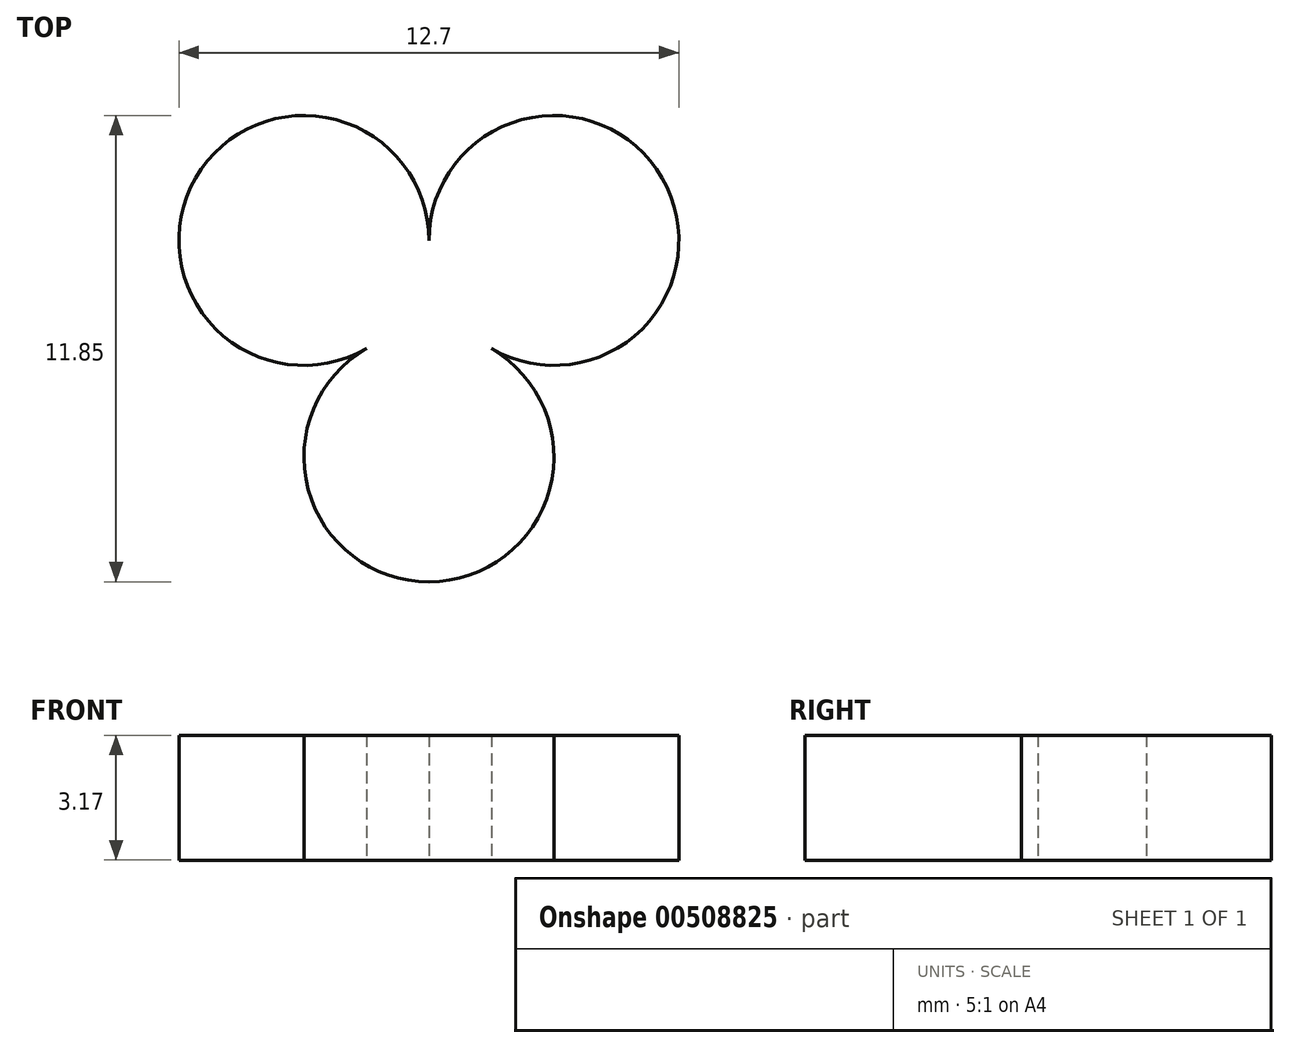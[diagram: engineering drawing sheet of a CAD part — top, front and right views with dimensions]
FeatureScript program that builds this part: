
annotation { "Feature Type Name" : "Feature", "Feature Type Description" : "" }
export const myFeature = defineFeature(function(context is Context, id is Id, definition is map)
    precondition{}
    {
        {
            var Q0;
            Q0=qCreatedBy(makeId("Right.planeOp"),FACE);
            var sketch = newSketch(context, id + "F0", { "sketchPlane" : qUnion([Q0])});
            skLineSegment(sketch, "E0", {"start": v(0, 0) * mm, "end": v(0, 179.6) * mm});
            skLineSegment(sketch, "E1", {"start": v(0, 179.6) * mm, "end": v(-169.33, -59.87) * mm});
            skLineSegment(sketch, "E2", {"start": v(-169.33, -59.87) * mm, "end": v(0, 0) * mm});
            skLineSegment(sketch, "E3", {"start": v(-169.33, -59.87) * mm, "end": v(84.67, -59.87) * mm, "construction": true});
            skLineSegment(sketch, "E4", {"start": v(0, 179.6) * mm, "end": v(84.67, -59.87) * mm, "construction": true});
            skLineSegment(sketch, "E5", {"start": v(0, 0) * mm, "end": v(84.67, -59.87) * mm, "construction": true});
            skLineSegment(sketch, "E6", {"start": v(0, 0) * mm, "end": v(0, -59.87) * mm, "construction": true});
            skCircle(sketch, "E7", {"center": v(-84.67, -59.87) * mm, "radius": 84.67 * mm, "construction": true});
            skCircle(sketch, "E8", {"center": v(0, -59.87) * mm, "radius": 84.67 * mm, "construction": true});
            skArc(sketch, "E9", {"start": v(-169.33, -59.87) * mm, "mid": v(-46.6, 32.96) * mm, "end": v(0, 179.6) * mm, "construction": true});
            skLineSegment(sketch, "E10", {"start": v(0, 179.6) * mm, "end": v(-254, 179.6) * mm, "construction": true});
            skLineSegment(sketch, "E11", {"start": v(-169.33, -59.87) * mm, "end": v(-254, 179.6) * mm, "construction": true});
            skSolve(sketch);
        }
        {
            var Q0;
            Q0=qCreatedBy(makeId("Right.planeOp"),FACE);
            var sketch = newSketch(context, id + "F1", { "sketchPlane" : qUnion([Q0])});
            skPoint(sketch, "E12.0", {"position": v(-254, 179.6) * mm});
            skPoint(sketch, "E13.0", {"position": v(-169.33, -59.87) * mm});
            skPoint(sketch, "E14.0", {"position": v(0, 0) * mm});
            skArc(sketch, "E15", {"start": v(-169.33, -59.87) * mm, "mid": v(-46.6, 32.96) * mm, "end": v(0, 179.6) * mm, "construction": true});
            skLineSegment(sketch, "E16", {"start": v(0, 179.6) * mm, "end": v(-254, 179.6) * mm, "construction": true});
            skLineSegment(sketch, "E17", {"start": v(-169.33, -59.87) * mm, "end": v(-254, 179.6) * mm, "construction": true});
            skCircle(sketch, "E18", {"center": v(-3.67, 0) * mm, "radius": 3.18 * mm, "construction": true});
            skCircle(sketch, "E19.1.0", {"center": v(1.83, -3.18) * mm, "radius": 3.18 * mm, "construction": true});
            skCircle(sketch, "E19.2.0", {"center": v(1.83, 3.18) * mm, "radius": 3.18 * mm, "construction": true});
            skLineSegment(sketch, "E20", {"start": v(1.83, 3.18) * mm, "end": v(1.83, -3.18) * mm, "construction": true});
            skLineSegment(sketch, "E21", {"start": v(-3.67, 0) * mm, "end": v(1.83, 0) * mm, "construction": true});
            skLineSegment(sketch, "E22", {"start": v(-3.67, 0) * mm, "end": v(-12.7, 0) * mm, "construction": true});
            skCircle(sketch, "E23", {"center": v(-12.7, 0) * mm, "radius": 3.18 * mm, "construction": true});
            skCircle(sketch, "E24.1.0", {"center": v(6.35, -11) * mm, "radius": 3.18 * mm, "construction": true});
            skCircle(sketch, "E24.2.0", {"center": v(6.35, 11) * mm, "radius": 3.18 * mm, "construction": true});
            skLineSegment(sketch, "E25", {"start": v(6.35, 11) * mm, "end": v(6.35, -11) * mm, "construction": true});
            skLineSegment(sketch, "E26", {"start": v(1.83, 0) * mm, "end": v(6.35, 0) * mm, "construction": true});
            skArc(sketch, "E27.0", {"start": v(-7.53, 135.81) * mm, "mid": v(-4.63, 157.62) * mm, "end": v(-3.67, 179.6) * mm});
            skLineSegment(sketch, "E28", {"start": v(-254, 179.6) * mm, "end": v(-32.17, 98.2) * mm, "construction": true});
            skLineSegment(sketch, "E29", {"start": v(-254, 179.6) * mm, "end": v(-7.53, 135.81) * mm, "construction": true});
            skLineSegment(sketch, "E30", {"start": v(-254, 179.6) * mm, "end": v(-49.83, 60.65) * mm, "construction": true});
            skLineSegment(sketch, "E31", {"start": v(-254, 179.6) * mm, "end": v(-73.8, 26.77) * mm, "construction": true});
            skArc(sketch, "E32", {"start": v(-175.24, -43.17) * mm, "mid": v(-61.07, 43.18) * mm, "end": v(-17.7, 179.6) * mm, "construction": true});
            skLineSegment(sketch, "E33", {"start": v(-73.8, 26.77) * mm, "end": v(-49.83, 60.65) * mm, "construction": true});
            skLineSegment(sketch, "E34", {"start": v(-49.83, 60.65) * mm, "end": v(-32.17, 98.2) * mm, "construction": true});
            skLineSegment(sketch, "E35", {"start": v(-32.17, 98.2) * mm, "end": v(-21.35, 138.27) * mm, "construction": true});
            skLineSegment(sketch, "E36", {"start": v(-21.35, 138.27) * mm, "end": v(-17.7, 179.6) * mm, "construction": true});
            skLineSegment(sketch, "E37", {"start": v(-254, 179.6) * mm, "end": v(-103.31, -2.4) * mm, "construction": true});
            skLineSegment(sketch, "E38", {"start": v(-73.8, 26.77) * mm, "end": v(-103.31, -2.4) * mm, "construction": true});
            skLineSegment(sketch, "E39", {"start": v(-254, 179.6) * mm, "end": v(-137.48, -25.96) * mm, "construction": true});
            skLineSegment(sketch, "E40", {"start": v(-175.24, -43.17) * mm, "end": v(-137.48, -25.96) * mm, "construction": true});
            skLineSegment(sketch, "E41", {"start": v(-103.31, -2.4) * mm, "end": v(-137.48, -25.96) * mm, "construction": true});
            skSolve(sketch);
        }
        {
            var Q0;
            Q0=qCreatedBy(makeId("Right.planeOp"),FACE);
            var sketch = newSketch(context, id + "F2", { "sketchPlane" : qUnion([Q0])});
            skPoint(sketch, "E42.0", {"position": v(-3.67, 179.6) * mm});
            skPoint(sketch, "E42.1", {"position": v(-7.53, 135.81) * mm});
            skPoint(sketch, "E42.2", {"position": v(-254, 179.6) * mm});
            skPoint(sketch, "E42.3", {"position": v(0, 0) * mm});
            skPoint(sketch, "E42.4", {"position": v(-12.7, 0) * mm});
            skArc(sketch, "E43", {"start": v(-7.53, 135.81) * mm, "mid": v(-4.63, 157.62) * mm, "end": v(-3.67, 179.6) * mm});
            skLineSegment(sketch, "E44", {"start": v(-7.53, 135.81) * mm, "end": v(-8.84, 128.42) * mm});
            skLineSegment(sketch, "E45", {"start": v(-8.18, 132.12) * mm, "end": v(-8.18, 84.63) * mm, "construction": true});
            skArc(sketch, "E46.1.0", {"start": v(-8.84, 128.42) * mm, "mid": v(-11.73, 106.61) * mm, "end": v(-12.7, 84.63) * mm});
            skPoint(sketch, "E46.center", {"position": v(-8.18, 132.12) * mm});
            skSolve(sketch);
        }
        {
            var Q0;
            Q0=qCreatedBy(makeId("Right.planeOp"),FACE);
            var sketch = newSketch(context, id + "F3", { "sketchPlane" : qUnion([Q0])});
            skPoint(sketch, "E47.0", {"position": v(0, 0) * mm});
            skPoint(sketch, "E48.0", {"position": v(-3.67, 179.6) * mm});
            skPoint(sketch, "E48.1", {"position": v(-7.53, 135.81) * mm});
            skPoint(sketch, "E48.2", {"position": v(-254, 179.6) * mm});
            skArc(sketch, "E49", {"start": v(-7.53, 135.81) * mm, "mid": v(-4.63, 157.62) * mm, "end": v(-3.67, 179.6) * mm});
            skLineSegment(sketch, "E50", {"start": v(-7.53, 135.81) * mm, "end": v(-21.54, 56.95) * mm});
            skLineSegment(sketch, "E51", {"start": v(-14.53, 96.38) * mm, "end": v(-14.53, 13.15) * mm, "construction": true});
            skArc(sketch, "E52.1.0", {"start": v(-21.54, 56.95) * mm, "mid": v(-24.43, 35.14) * mm, "end": v(-25.4, 13.15) * mm});
            skPoint(sketch, "E52.center", {"position": v(-14.53, 96.38) * mm});
            skLineSegment(sketch, "E53", {"start": v(0, 0) * mm, "end": v(-25.4, 0) * mm, "construction": true});
            skSolve(sketch);
        }
        {
            var Q0;
            Q0=sQuery(id+"F0.wireOp",VERTEX,"E8.center");
            var Q1;
            Q1=qCreatedBy(makeId("Top.planeOp"),FACE);
            cPlane(context, id + "F4", {"entities" : qUnion([Q0, Q1]), "cplaneType" : CPlaneType.PLANE_POINT, "offset" : 25.4 * mm, "width" : 152.4 * mm, "height" : 152.4 * mm});
        }
        {
            var Q0;
            Q0=qCreatedBy(id+"F4.planeOp",FACE);
            var sketch = newSketch(context, id + "F5", { "sketchPlane" : qUnion([Q0])});
            skCircle(sketch, "E54.cCircle", {"center": v(0, 0) * mm, "radius": 169.33 * mm, "construction": true});
            skLineSegment(sketch, "E54.0", {"start": v(0, -169.33) * mm, "end": v(-146.65, 84.67) * mm, "construction": true});
            skLineSegment(sketch, "E54.1", {"start": v(-146.65, 84.67) * mm, "end": v(146.65, 84.67) * mm, "construction": true});
            skLineSegment(sketch, "E54.2", {"start": v(146.65, 84.67) * mm, "end": v(0, -169.33) * mm, "construction": true});
            skSolve(sketch);
        }
        {
            var Q0;
            Q0=sQuery(id+"F0.wireOp",VERTEX,"E6.start");
            var Q1;
            Q1=sQuery(id+"F5.wireOp",VERTEX,"E54.1.start");
            var Q2;
            Q2=sQuery(id+"F5.wireOp",VERTEX,"E54.2.start");
            cPlane(context, id + "F6", {"entities" : qUnion([Q0, Q1, Q2]), "cplaneType" : CPlaneType.THREE_POINT, "offset" : 25.4 * mm, "width" : 152.4 * mm, "height" : 152.4 * mm});
        }
        {
            var Q0;
            Q0=qCreatedBy(id+"F6.planeOp",FACE);
            var sketch = newSketch(context, id + "F7", { "sketchPlane" : qUnion([Q0])});
            skLineSegment(sketch, "E55", {"start": v(-146.65, 103.7) * mm, "end": v(0, 0) * mm});
            skLineSegment(sketch, "E56", {"start": v(0, 0) * mm, "end": v(146.65, 103.7) * mm});
            skLineSegment(sketch, "E57", {"start": v(146.65, 103.7) * mm, "end": v(-146.65, 103.7) * mm});
            skLineSegment(sketch, "E58", {"start": v(0, 103.7) * mm, "end": v(0, 0) * mm});
            skSolve(sketch);
        }
        {
            var Q0;
            Q0=sQuery(id+"F7.wireOp",VERTEX,"E57.end");
            var Q1;
            Q1=sQuery(id+"F7.wireOp",VERTEX,"E57.start");
            var Q2;
            Q2=sQuery(id+"F0.wireOp",VERTEX,"E4.start");
            cPlane(context, id + "F8", {"entities" : qUnion([Q0, Q1, Q2]), "cplaneType" : CPlaneType.THREE_POINT, "offset" : 25.4 * mm, "width" : 152.4 * mm, "height" : 152.4 * mm});
        }
        {
            var Q0;
            Q0=sQuery(id+"F1.wireOp",VERTEX,"E27.0.end");
            var Q1;
            Q1=qCreatedBy(makeId("Top.planeOp"),FACE);
            cPlane(context, id + "F9", {"entities" : qUnion([Q0, Q1]), "cplaneType" : CPlaneType.PLANE_POINT, "offset" : 25.4 * mm, "width" : 152.4 * mm, "height" : 152.4 * mm});
        }
        {
            var Q0;
            Q0=qCreatedBy(id+"F9.planeOp",FACE);
            var sketch = newSketch(context, id + "F10", { "sketchPlane" : qUnion([Q0])});
            skPoint(sketch, "E59.0", {"position": v(0, -3.67) * mm});
            skCircle(sketch, "E60", {"center": v(0, -3.67) * mm, "radius": 3.18 * mm});
            skCircle(sketch, "E61.1.0", {"center": v(3.18, 1.83) * mm, "radius": 3.18 * mm});
            skCircle(sketch, "E61.2.0", {"center": v(-3.18, 1.83) * mm, "radius": 3.18 * mm});
            skPoint(sketch, "E61.center", {"position": v(0, 0) * mm});
            skSolve(sketch);
        }
        {
            var Q0;
            Q0=qCreatedBy(makeId("Top.planeOp"),FACE);
            var sketch = newSketch(context, id + "F11", { "sketchPlane" : qUnion([Q0])});
            skCircle(sketch, "E62", {"center": v(-6.35, -11) * mm, "radius": 3.18 * mm});
            skCircle(sketch, "E63", {"center": v(-25.4, 0) * mm, "radius": 3.18 * mm});
            skCircle(sketch, "E64.1.0", {"center": v(12.7, 0) * mm, "radius": 3.18 * mm});
            skCircle(sketch, "E64.2.0", {"center": v(-6.35, 11) * mm, "radius": 3.18 * mm});
            skPoint(sketch, "E64.center", {"position": v(0, 0) * mm});
            skCircle(sketch, "E65.1.0", {"center": v(12.7, -22) * mm, "radius": 3.18 * mm});
            skCircle(sketch, "E65.2.0", {"center": v(12.7, 22) * mm, "radius": 3.18 * mm});
            skLineSegment(sketch, "E66", {"start": v(0, 0) * mm, "end": v(12.7, 0) * mm});
            skLineSegment(sketch, "E67", {"start": v(0, 0) * mm, "end": v(-25.4, 0) * mm});
            skSolve(sketch);
        }
        {
            var Q0;
            Q0=qSketchRegion(id+"F10",true);
            extrude(context, id + "F12", {"entities" : qUnion([Q0]), "depth" : 3.17 * mm, "offsetDistance" : 25.4 * mm});
        }
    });
